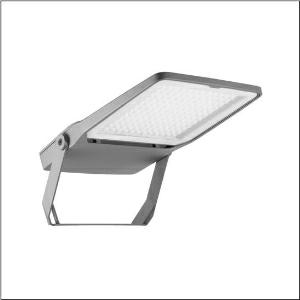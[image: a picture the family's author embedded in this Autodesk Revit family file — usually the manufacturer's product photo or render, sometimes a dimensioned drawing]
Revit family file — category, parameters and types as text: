
# Revit family: floodlight_fl_20_midi___pl52_5xa7682d3d1ac_4da3
name_source: partatom
category: Lighting Fixtures
units: mm (PartAtom-declared; Revit-internal decimal feet)

## family parameters
Cut with Voids When Loaded = No
Host = Face
Light Source = No
Part Type = Normal
Room Calculation Point = No
Round Connector Dimension = Use Diameter
Shared = No

## types (1)
- --- (1 x LED 5000K / CRI = 70 (unbekannt), 18250 lm, 5000K)
    Apparent Load = 142 VA
    CIE Flux Codes = 27 59 98 100 100
    Color Rendering = 70
    Color Temperature = 5000K
    Default Elevation = 1800 mm
    Description = Floodlight FL 20 midi, floodlight, primary light control with lens, of plastic, primary optical cover: protective disc, of toughened safety glass, transparent, light distribution: PL52, light emission: direct distribution, primary light characteristic: asymmetric, installation type: surface-mounted, LED, High Power LED, rated luminous flux: 18.250lm, luminous efficacy: 129lm/W, light colour: 750, colour temperature: 5000K, control gear: ECG Plus, control: flexible luminous flux parameterisation, time-dependent luminous flux control, digital communication interface, power reduction, overheat protection, electronic power reduction, with terminal, 5-pole, max. 2.5mm², mains connection: 220..240V, AC, 50/60Hz, rated input power: 142W, LED unit, of diecast aluminium, powder-coated, Siteco® metallic grey (DB 702S), corrosivity category C5 mid according to DIN EN ISO 12944, incl. 1x M20 cable gland for cable Ø 6.5..12mm, length: 654mm, width: 450mm, height: 76mm, housing frame, of diecast aluminium, powder-coated, Siteco® metallic grey (DB 702S), mounting bracket, of steel, powder-coated, Siteco® metallic grey (DB 702S), DALI, protection rating (complete): IP66, insulation class (complete): insulation class II (safety insulation), certification: CE, ENEC, VDE, protection symbol: D, permissible operating ambient temperature: -40..+40°C, permissible operating ambient temperature for outdoor applications: -40..+50°C, standard: DIN EN 12944, packaging unit: 1 piece

Light Distribution: PL52
    Height = 76 mm
    Lamp = 1 x LED 5000K / CRI >= 70 (unbekannt)
    Lamp Light Flux = 18250 lm
    Lamp count = 1
    Length = 672 mm
    Luminous efficacy = 129 lm/W
    Manufacturer = Siteco
    ModVariant = No
    Model = 5XA7682D3D1AC
    Mounting Place = Wall
    Mounting Type = Surface mounted
    Number of Poles = 1
    OnlyDefault = Yes
    Power Factor = 1
    Product Name = Floodlight FL 20 midi | PL52
    Product group = floodlight | wall mounted
    ProductGroupID = 2001
    Protection Class = Protection class II
    Protection Degree = IP 66
    RLX_Detail_Level = 1
    RLX_Emergency_Light_Flux = 0 lm
    RLX_Emergency_Type = 0
    RLX_Emergency_Type_DB = No
    RlxData = <blob elided: 97809 chars, md5=ad7d725a>
    Socket = socket
    Standby Power = 0 W
    System Light Flux = 18250 lm
    System Power = 142 W
    Type Comments = factory setting: luminous flux: 100 % | dim-lin: 254 | 489 mA
    Type Image = l_1005943.jpg
    URL = http://relux.com
    VarID = @adj_147823
    Voltage = 0 V
    Weight = 0.00 kg
    Width = 450 mm

## geometry (parser evidence)
native form markers: Blend x4, Sweep x12
no freeform markers — native parametric forms only
